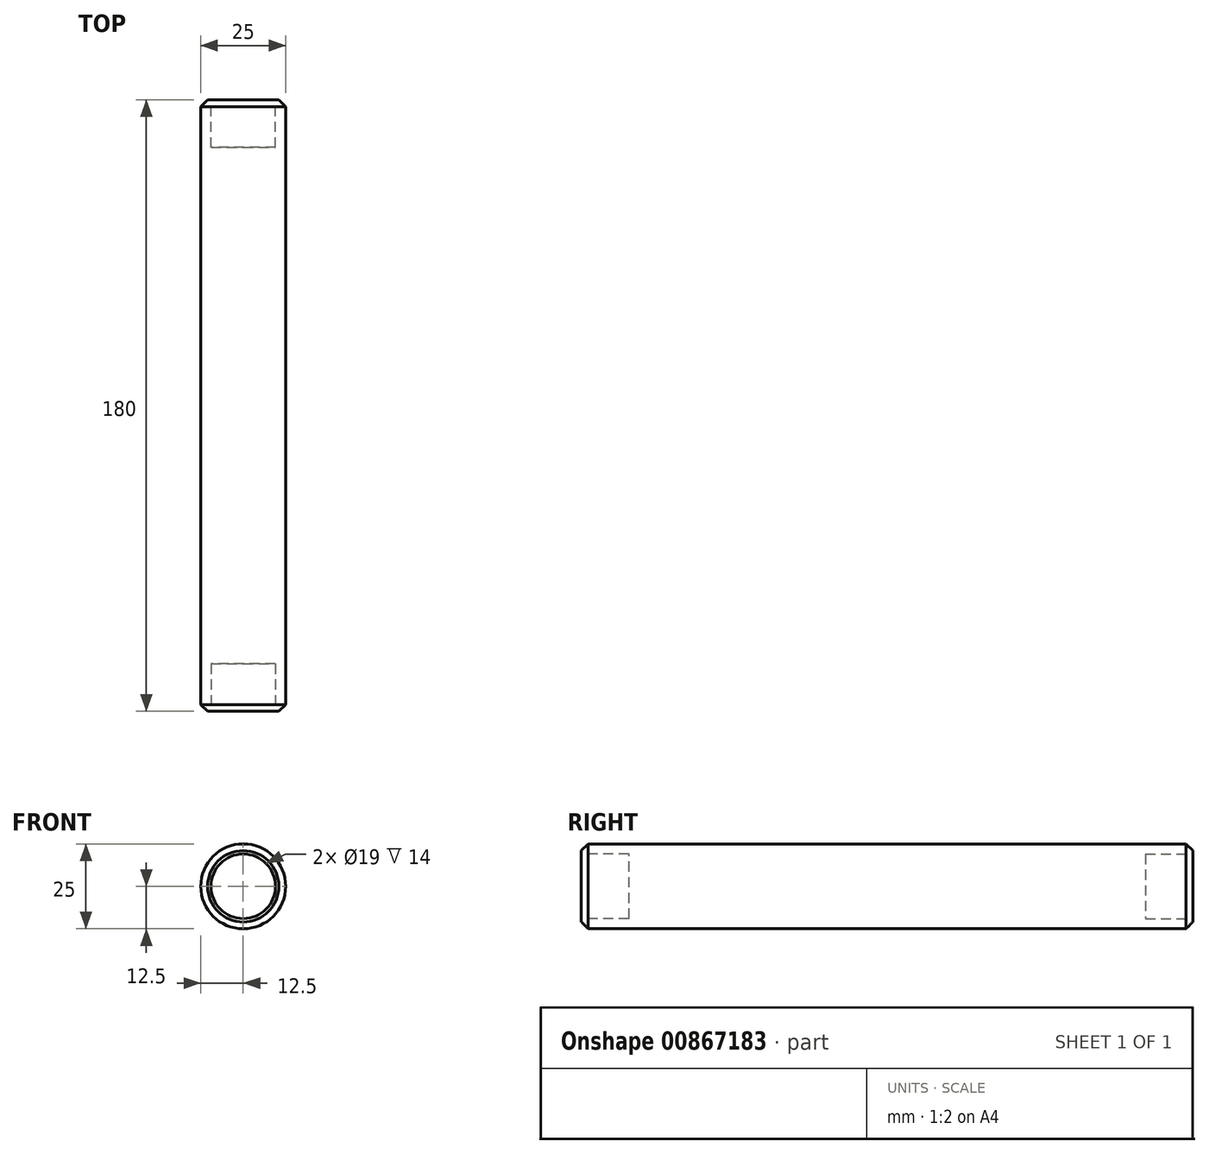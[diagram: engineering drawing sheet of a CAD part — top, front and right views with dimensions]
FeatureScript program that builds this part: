
annotation { "Feature Type Name" : "Feature", "Feature Type Description" : "" }
export const myFeature = defineFeature(function(context is Context, id is Id, definition is map)
    precondition{}
    {
        {
            var Q0;
            Q0=qCreatedBy(makeId("Front.planeOp"),FACE);
            var sketch = newSketch(context, id + "F0", { "sketchPlane" : qUnion([Q0])});
            skCircle(sketch, "E0", {"center": v(0, 0) * mm, "radius": 12.5 * mm});
            skSolve(sketch);
        }
        {
            var Q0;
            Q0=makeQuery(id+"F0.imprint","IMPRINT",FACE,{"disambiguationData":[TD([[makeQuery(id+"F0.imprint","IMPRINT",EDGE,{"derivedFrom":sQuery(id+"F0.wireOp",EDGE,"E0")}),1.0]])]});
            extrude(context, id + "F1", {"entities" : qUnion([Q0]), "depth" : 90 * mm, "offsetDistance" : 25 * mm, "hasSecondDirection" : true, "secondDirectionOppositeDirection" : true, "secondDirectionDepth" : 90 * mm});
        }
        {
            var Q0;
            Q0=makeQuery(id+"F1.opExtrude","CAP_FACE",FACE,{"disambiguationData":[OSD([sQuery(id+"F0.wireOp",EDGE,"E0")])],"isStart":false});
            var sketch = newSketch(context, id + "F2", { "sketchPlane" : qUnion([Q0])});
            skCircle(sketch, "E1", {"center": v(0, 0) * mm, "radius": 9.5 * mm});
            skSolve(sketch);
        }
        {
            var Q0;
            Q0=makeQuery(id+"F2.imprint","IMPRINT",FACE,{"disambiguationData":[TD([[makeQuery(id+"F2.imprint","IMPRINT",EDGE,{"derivedFrom":sQuery(id+"F2.wireOp",EDGE,"E1")}),1.0]])]});
            extrude(context, id + "F3", {"entities" : qUnion([Q0]), "operationType" : NewBodyOperationType.REMOVE, "oppositeDirection" : true, "depth" : 14 * mm, "offsetDistance" : 25 * mm});
        }
        {
            var Q0;
            Q0=makeQuery(id+"F1.opExtrude","CAP_EDGE",EDGE,{"disambiguationData":[OSD([sQuery(id+"F0.wireOp",EDGE,"E0")])],"isStart":false});
            chamfer(context, id + "F4", {"entities" : qUnion([Q0]), "width" : 2 * mm, "tangentPropagation" : true});
        }
        {
            var Q0;
            Q0=makeQuery(id+"F1.opExtrude","CAP_FACE",FACE,{"disambiguationData":[OSD([sQuery(id+"F0.wireOp",EDGE,"E0")])],"isStart":true});
            var sketch = newSketch(context, id + "F5", { "sketchPlane" : qUnion([Q0])});
            skCircle(sketch, "E2", {"center": v(0, 0) * mm, "radius": 9.5 * mm});
            skSolve(sketch);
        }
        {
            var Q0;
            Q0=makeQuery(id+"F5.imprint","IMPRINT",FACE,{"disambiguationData":[TD([[makeQuery(id+"F5.imprint","IMPRINT",EDGE,{"derivedFrom":sQuery(id+"F5.wireOp",EDGE,"E2")}),1.0]])]});
            extrude(context, id + "F6", {"entities" : qUnion([Q0]), "operationType" : NewBodyOperationType.REMOVE, "oppositeDirection" : true, "depth" : 14 * mm, "offsetDistance" : 25 * mm});
        }
        {
            var Q0;
            Q0=makeQuery(id+"F1.opExtrude","CAP_EDGE",EDGE,{"disambiguationData":[OSD([sQuery(id+"F0.wireOp",EDGE,"E0")])],"isStart":true});
            chamfer(context, id + "F7", {"entities" : qUnion([Q0]), "width" : 2 * mm, "tangentPropagation" : true});
        }
    });
